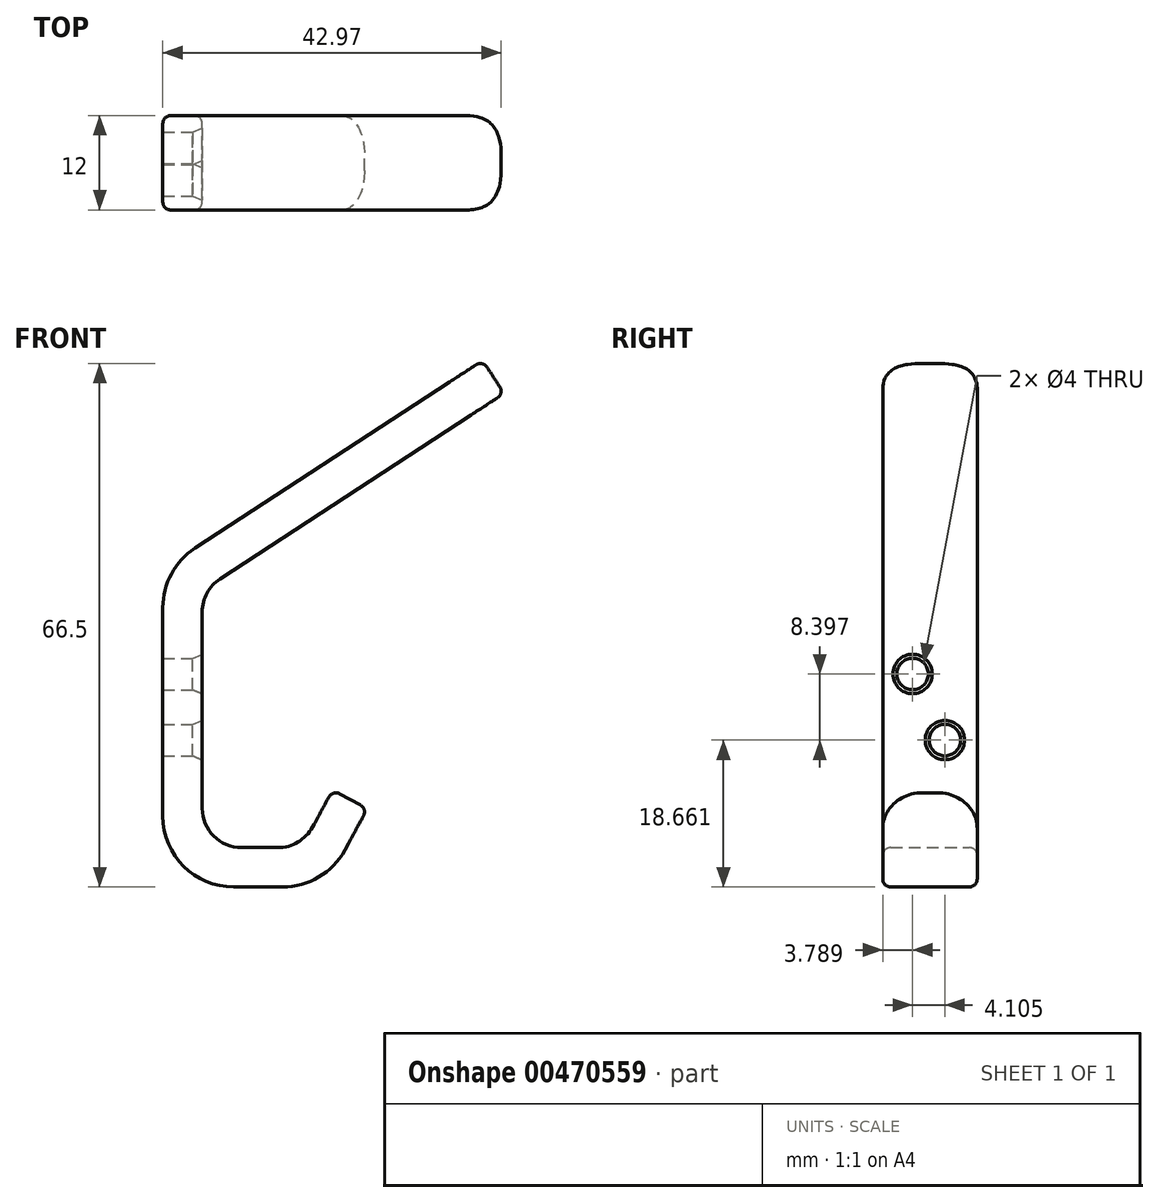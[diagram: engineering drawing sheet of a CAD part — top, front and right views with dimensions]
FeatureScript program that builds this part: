
annotation { "Feature Type Name" : "Feature", "Feature Type Description" : "" }
export const myFeature = defineFeature(function(context is Context, id is Id, definition is map)
    precondition{}
    {
        {
            var Q0;
            Q0=qCreatedBy(makeId("Front.planeOp"),FACE);
            var sketch = newSketch(context, id + "F0", { "sketchPlane" : qUnion([Q0])});
            skLineSegment(sketch, "E0", {"start": v(0, 0) * mm, "end": v(0, 40.37) * mm});
            skLineSegment(sketch, "E1", {"start": v(0, 40.37) * mm, "end": v(40.62, 66.89) * mm});
            skLineSegment(sketch, "E2", {"start": v(0, 0) * mm, "end": v(20.56, 0) * mm});
            skLineSegment(sketch, "E3", {"start": v(20.56, 0) * mm, "end": v(25.97, 9.92) * mm});
            skLineSegment(sketch, "E4", {"start": v(25.97, 9.92) * mm, "end": v(21.58, 12.32) * mm});
            skPoint(sketch, "E5.endSnap0", {"position": v(0, 20.19) * mm});
            skPoint(sketch, "E6.orphan", {"position": v(-8.55, 9.92) * mm});
            skPoint(sketch, "E7.end.orphan", {"position": v(-8.55, -0.53) * mm});
            skPoint(sketch, "E8.end.orphan", {"position": v(19.81, 3.95) * mm});
            skPoint(sketch, "E5.end.orphan", {"position": v(6.16, 20.19) * mm});
            skPoint(sketch, "E5.start.orphan", {"position": v(0, 20.19) * mm});
            skLineSegment(sketch, "E9.0", {"start": v(5, 37.66) * mm, "end": v(43.35, 62.7) * mm});
            skLineSegment(sketch, "E9.1", {"start": v(5, 5) * mm, "end": v(5, 37.66) * mm});
            skLineSegment(sketch, "E10.0", {"start": v(5, 5) * mm, "end": v(18.47, 5) * mm});
            skLineSegment(sketch, "E11.0", {"start": v(17.6, 5) * mm, "end": v(21.58, 12.32) * mm});
            skPoint(sketch, "E12.orphan", {"position": v(19.81, 13.28) * mm});
            skLineSegment(sketch, "E13", {"start": v(40.62, 66.89) * mm, "end": v(43.35, 62.7) * mm});
            skSolve(sketch);
        }
        {
            var Q0;
            Q0=makeQuery(id+"F0.imprint","IMPRINT",FACE,{"disambiguationData":[TD([[makeQuery(id+"F0.imprint","IMPRINT",EDGE,{"derivedFrom":sQuery(id+"F0.wireOp",EDGE,"E0")}),-1.0]])]});
            extrude(context, id + "F1", {"entities" : qUnion([Q0]), "depth" : 12 * mm});
        }
        {
            var Q0;
            Q0=makeQuery(id+"F1.opExtrude","SWEPT_EDGE",EDGE,{"disambiguationData":[OSD([sQuery(id+"F0.wireOp",EDGE,"E2"),sQuery(id+"F0.wireOp",EDGE,"E3")])]});
            fillet(context, id + "F2", {"entities" : qUnion([Q0]), "radius" : 9 * mm, "tangentPropagation" : true, "defaultsChanged" : false, "vertexSettings" : [], "allowEdgeOverflow" : false});
        }
        {
            var Q0;
            Q0=makeQuery(id+"F1.opExtrude","SWEPT_EDGE",EDGE,{"disambiguationData":[OSD([sQuery(id+"F0.wireOp",EDGE,"E10.0"),sQuery(id+"F0.wireOp",EDGE,"E11.0")])]});
            fillet(context, id + "F3", {"entities" : qUnion([Q0]), "radius" : 5 * mm, "tangentPropagation" : true, "allowEdgeOverflow" : false});
        }
        {
            var Q0;
            Q0=makeQuery(id+"F1.opExtrude","SWEPT_EDGE",EDGE,{"disambiguationData":[OSD([sQuery(id+"F0.wireOp",EDGE,"E0"),sQuery(id+"F0.wireOp",EDGE,"E1")])]});
            fillet(context, id + "F4", {"entities" : qUnion([Q0]), "radius" : 9 * mm, "tangentPropagation" : true, "allowEdgeOverflow" : false});
        }
        {
            var Q0;
            Q0=makeQuery(id+"F1.opExtrude","SWEPT_EDGE",EDGE,{"disambiguationData":[OSD([sQuery(id+"F0.wireOp",EDGE,"E9.0"),sQuery(id+"F0.wireOp",EDGE,"E9.1")])]});
            fillet(context, id + "F5", {"entities" : qUnion([Q0]), "radius" : 5 * mm, "tangentPropagation" : true, "allowEdgeOverflow" : false});
        }
        {
            var Q0;
            Q0=makeQuery(id+"F1.opExtrude","CAP_EDGE",EDGE,{"disambiguationData":[OSD([sQuery(id+"F0.wireOp",EDGE,"E4")])],"isStart":false});
            fillet(context, id + "F6", {"entities" : qUnion([Q0]), "radius" : 5 * mm, "tangentPropagation" : true, "allowEdgeOverflow" : false});
        }
        {
            var Q0;
            Q0=makeQuery(id+"F1.opExtrude","CAP_EDGE",EDGE,{"disambiguationData":[OSD([sQuery(id+"F0.wireOp",EDGE,"E4")])],"isStart":true});
            fillet(context, id + "F7", {"entities" : qUnion([Q0]), "radius" : 5 * mm, "tangentPropagation" : true, "defaultsChanged" : false, "vertexSettings" : [], "allowEdgeOverflow" : false});
        }
        {
            var Q0;
            Q0=makeQuery(id+"F1.opExtrude","CAP_EDGE",EDGE,{"disambiguationData":[OSD([sQuery(id+"F0.wireOp",EDGE,"E13")])],"isStart":false});
            var Q1;
            Q1=makeQuery(id+"F1.opExtrude","CAP_EDGE",EDGE,{"disambiguationData":[OSD([sQuery(id+"F0.wireOp",EDGE,"E13")])],"isStart":true});
            fillet(context, id + "F8", {"entities" : qUnion([Q0, Q1]), "radius" : 5 * mm, "tangentPropagation" : true, "rho" : .5, "crossSection" : FilletCrossSection.CONIC, "allowEdgeOverflow" : false});
        }
        {
            var Q0;
            Q0=makeQuery(id+"F1.opExtrude","SWEPT_FACE",FACE,{"disambiguationData":[OSD([sQuery(id+"F0.wireOp",EDGE,"E9.1")])]});
            var sketch = newSketch(context, id + "F9", { "sketchPlane" : qUnion([Q0])});
            skSolve(sketch);
        }
        {
            var Q0;
            Q0=makeQuery(id+"F1.opExtrude","SWEPT_EDGE",EDGE,{"disambiguationData":[OSD([sQuery(id+"F0.wireOp",EDGE,"E9.1"),sQuery(id+"F0.wireOp",EDGE,"E10.0")])]});
            fillet(context, id + "F10", {"entities" : qUnion([Q0]), "radius" : 5 * mm, "tangentPropagation" : true, "allowEdgeOverflow" : false});
        }
        {
            var Q0;
            Q0=makeQuery(id+"F1.opExtrude","SWEPT_EDGE",EDGE,{"disambiguationData":[OSD([sQuery(id+"F0.wireOp",EDGE,"E0"),sQuery(id+"F0.wireOp",EDGE,"E2")])]});
            fillet(context, id + "F11", {"entities" : qUnion([Q0]), "radius" : 9 * mm, "tangentPropagation" : true, "allowEdgeOverflow" : false});
        }
        {
            var Q0;
            {var subQ0=sQuery(id+"F0.wireOp",EDGE,"E9.1");Q0=makeQuery(id+"F9.imprint","IMPRINT",FACE,{"disambiguationData":[TD([[makeQuery(id+"F9.imprint","IMPRINT",EDGE,{"derivedFrom":makeQuery(id+"F1.opExtrude","CAP_EDGE",EDGE,{"disambiguationData":[OSD([subQ0])],"isStart":true})}),1.0]])]});}
            var sketch = newSketch(context, id + "F12", { "sketchPlane" : qUnion([Q0])});
            skCircle(sketch, "E14", {"center": v(-8.21, 27.06) * mm, "radius": 2.18 * mm});
            skCircle(sketch, "E15", {"center": v(-4.1, 18.66) * mm, "radius": 2.34 * mm});
            skSolve(sketch);
        }
        {
            var Q0;
            Q0=sQuery(id+"F12.wireOp",VERTEX,"E14.center");
            var Q1;
            Q1=makeQuery(id+"F1.opExtrude","SWEPT_BODY",BODY,{"disambiguationData":[OSD([sQuery(id+"F0.wireOp",EDGE,"E0"),sQuery(id+"F0.wireOp",EDGE,"E1"),sQuery(id+"F0.wireOp",EDGE,"E2"),sQuery(id+"F0.wireOp",EDGE,"E3"),sQuery(id+"F0.wireOp",EDGE,"E4"),sQuery(id+"F0.wireOp",EDGE,"E9.0"),sQuery(id+"F0.wireOp",EDGE,"E9.1"),sQuery(id+"F0.wireOp",EDGE,"E10.0"),sQuery(id+"F0.wireOp",EDGE,"E11.0"),sQuery(id+"F0.wireOp",EDGE,"E13")])]});
            hole(context, id + "F13", {"style" : HoleStyle.C_SINK, "endStyle" : HoleEndStyle.THROUGH, "holeDiameter" : 4 * mm, "cSinkDiameter" : 5 * mm, "cSinkAngle" : 45 * degree, "isTappedThrough" : true, "tappedDepth" : 12 * mm, "tapClearance" : 3, "locations" : qUnion([Q0]), "scope" : qUnion([Q1])});
        }
        {
            var Q0;
            Q0=sQuery(id+"F12.wireOp",VERTEX,"E15.center");
            var Q1;
            Q1=makeQuery(id+"F1.opExtrude","SWEPT_BODY",BODY,{"disambiguationData":[OSD([sQuery(id+"F0.wireOp",EDGE,"E0"),sQuery(id+"F0.wireOp",EDGE,"E1"),sQuery(id+"F0.wireOp",EDGE,"E2"),sQuery(id+"F0.wireOp",EDGE,"E3"),sQuery(id+"F0.wireOp",EDGE,"E4"),sQuery(id+"F0.wireOp",EDGE,"E9.0"),sQuery(id+"F0.wireOp",EDGE,"E9.1"),sQuery(id+"F0.wireOp",EDGE,"E10.0"),sQuery(id+"F0.wireOp",EDGE,"E11.0"),sQuery(id+"F0.wireOp",EDGE,"E13")])]});
            hole(context, id + "F14", {"style" : HoleStyle.C_SINK, "endStyle" : HoleEndStyle.THROUGH, "holeDiameter" : 4 * mm, "cSinkDiameter" : 5 * mm, "cSinkAngle" : 45 * degree, "isTappedThrough" : true, "tappedDepth" : 12 * mm, "tapClearance" : 3, "locations" : qUnion([Q0]), "scope" : qUnion([Q1])});
        }
        {
            var Q0;
            Q0=makeQuery(id+"F1.opExtrude","CAP_FACE",FACE,{"disambiguationData":[OSD([sQuery(id+"F0.wireOp",EDGE,"E0"),sQuery(id+"F0.wireOp",EDGE,"E1"),sQuery(id+"F0.wireOp",EDGE,"E2"),sQuery(id+"F0.wireOp",EDGE,"E3"),sQuery(id+"F0.wireOp",EDGE,"E4"),sQuery(id+"F0.wireOp",EDGE,"E9.0"),sQuery(id+"F0.wireOp",EDGE,"E9.1"),sQuery(id+"F0.wireOp",EDGE,"E10.0"),sQuery(id+"F0.wireOp",EDGE,"E11.0"),sQuery(id+"F0.wireOp",EDGE,"E13")])],"isStart":false});
            fillet(context, id + "F15", {"entities" : qUnion([Q0]), "radius" : 1 * mm, "tangentPropagation" : true, "defaultsChanged" : false, "vertexSettings" : [], "allowEdgeOverflow" : false});
        }
    });
